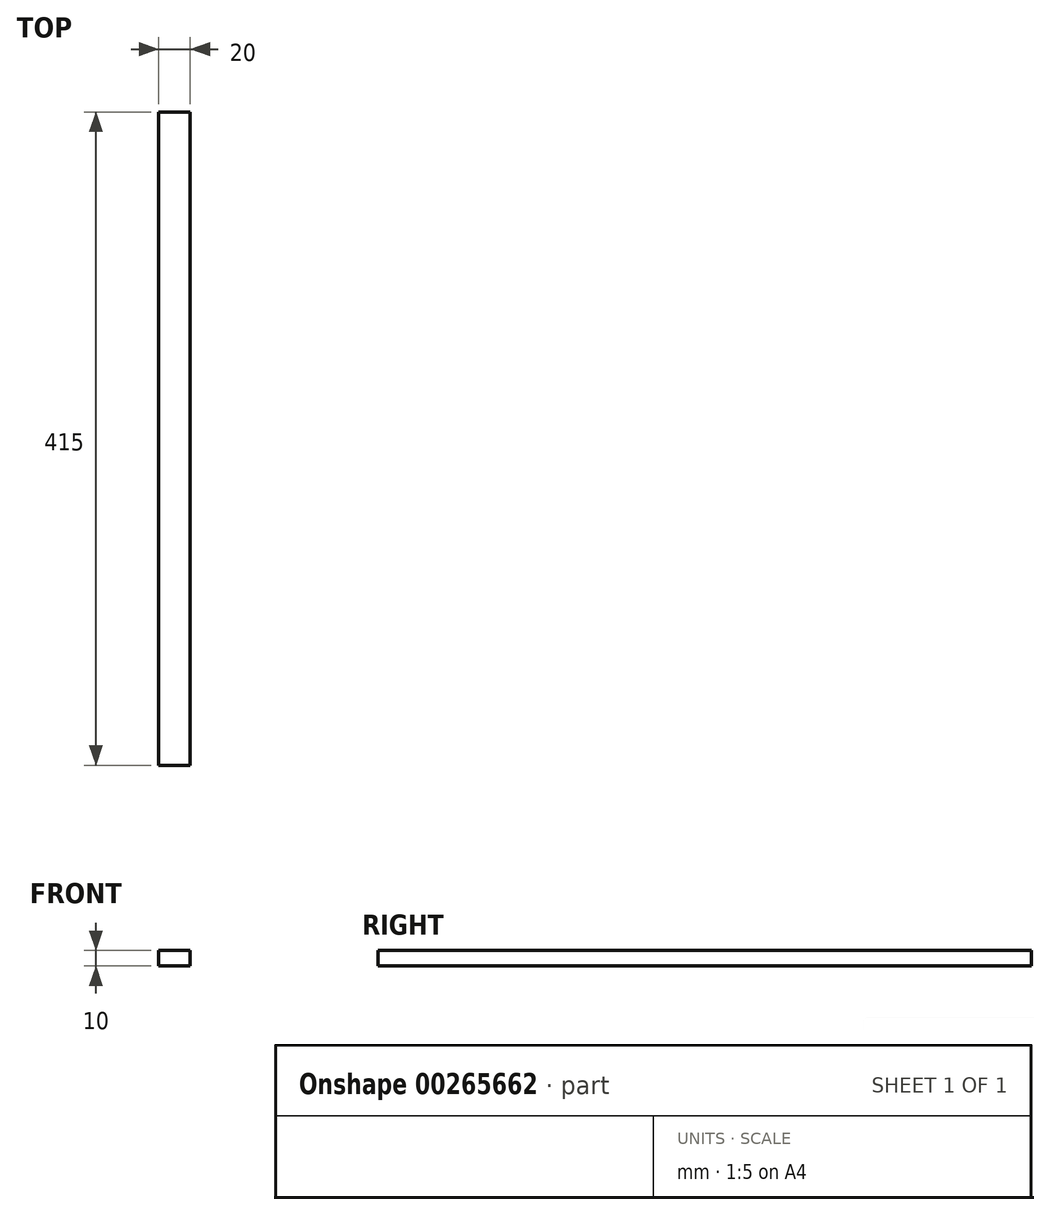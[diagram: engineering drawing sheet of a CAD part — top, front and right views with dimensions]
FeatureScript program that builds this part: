
annotation { "Feature Type Name" : "Feature", "Feature Type Description" : "" }
export const myFeature = defineFeature(function(context is Context, id is Id, definition is map)
    precondition{}
    {
        {
            var Q0;
            Q0=qCreatedBy(makeId("Front.planeOp"),FACE);
            var sketch = newSketch(context, id + "F0", { "sketchPlane" : qUnion([Q0])});
            skLineSegment(sketch, "E0.bottom", {"start": v(0, 0) * mm, "end": v(20, 0) * mm});
            skLineSegment(sketch, "E0.top", {"start": v(0, -10) * mm, "end": v(20, -10) * mm});
            skLineSegment(sketch, "E0.left", {"start": v(0, 0) * mm, "end": v(0, -10) * mm});
            skLineSegment(sketch, "E0.right", {"start": v(20, 0) * mm, "end": v(20, -10) * mm});
            skSolve(sketch);
        }
        {
            var Q0;
            Q0=qSketchRegion(id+"F0",true);
            extrude(context, id + "F1", {"entities" : qUnion([Q0]), "depth" : 415 * mm});
        }
    });
